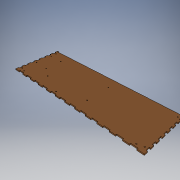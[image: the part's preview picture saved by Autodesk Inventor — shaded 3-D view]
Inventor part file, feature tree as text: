
AUTODESK INVENTOR PART (.ipt)
format: ipt  version: 2018.3 (Build 223284000, 284)  size: 460,288 bytes
history: native  units: mm
features: other x12, reference x7, extrude x4, sketch x4
ambient origin geometry x8: Origin, YZ Plane, XZ Plane, XY Plane, X Axis, Y Axis, Z Axis, Center Point
bodies: Solido1 (feature_tree)
feature tree (27):
  extrude  "Estrusione1"  Depth=467.0mm
  extrude  "Estrusione2"  Depth=157.0mm
  extrude  "Estrusione3"  Depth=4.0mm TaperAngle=0.0deg
  extrude  "Estrusione4"  Depth=4.0mm
  sketch  "Schizzo1"
  sketch  "Schizzo3"
  other  "Linea chiusa proiettata2"
  sketch  "Schizzo4"
  reference  "Riferimento1"
  reference  "Riferimento2"
  reference  "Riferimento3"
  reference  "Riferimento4"
  reference  "Riferimento5"
  reference  "Riferimento6"
  reference  "Riferimento7"
  sketch  "Schizzo5"
  other  "Linea chiusa proiettata3"
  other  "<userpath>\Desktop\Scorbot Hardware\Case Board\caseHw.iam"
  other  "caseHw.iam"
  other  "matherBoard v1:1"
  other  "PCB Component:1"
  other  "Board:1"
  other  "Raspberry Pi 3:1"
  other  "Raspberry Pi 347_115"
  other  "Raspberry Pi 345_113"
  other  "Raspberry Pi 349_117"
  other  "Raspberry Pi 351_119"
